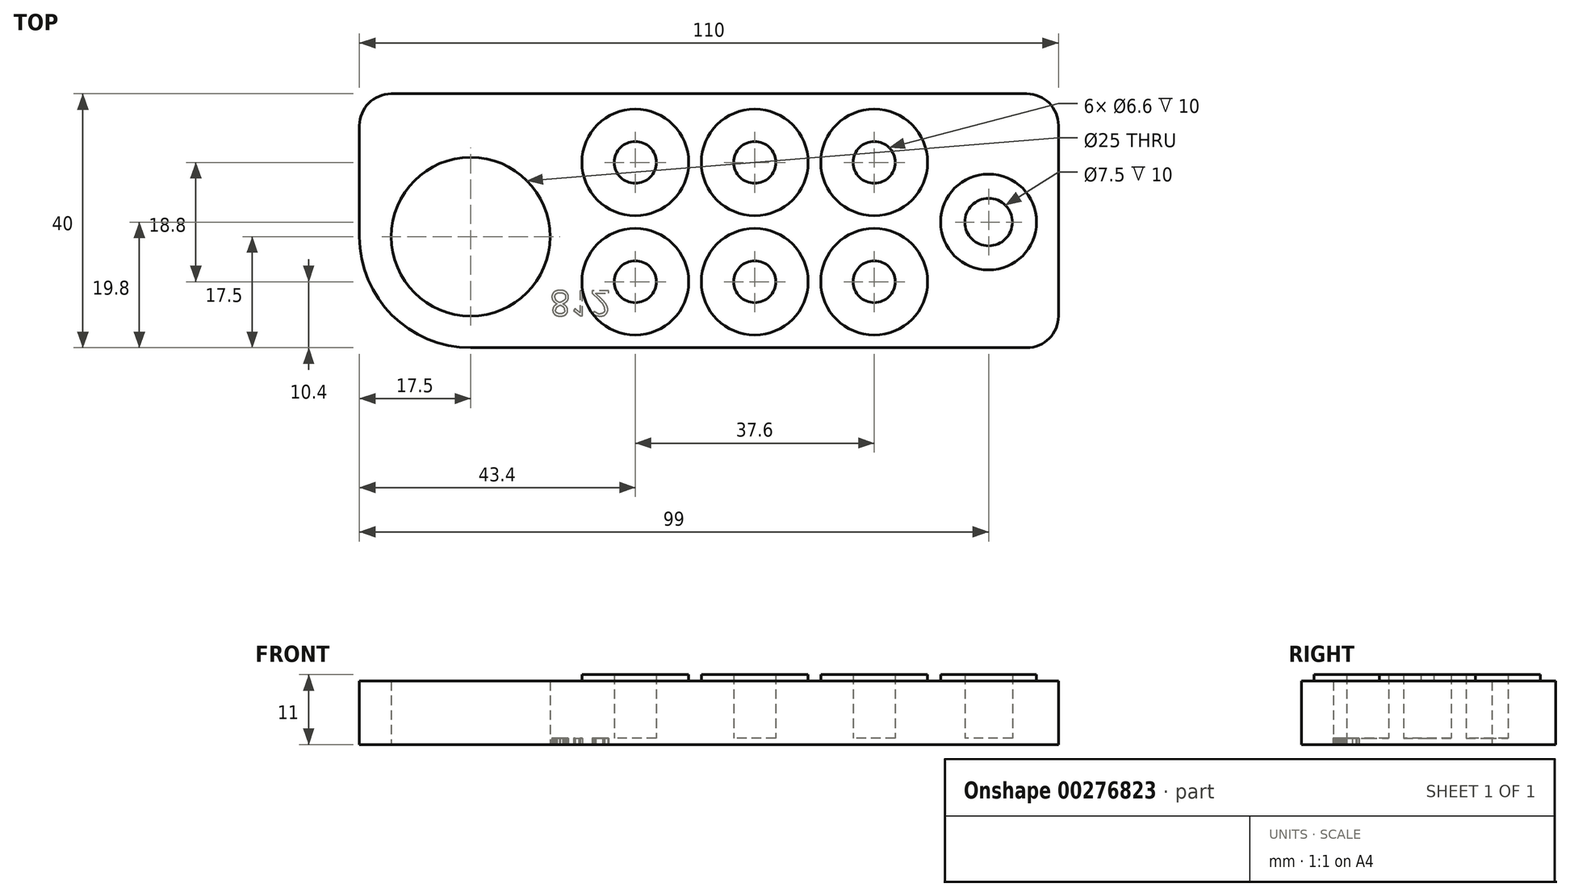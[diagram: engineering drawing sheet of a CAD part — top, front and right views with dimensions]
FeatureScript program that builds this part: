
annotation { "Feature Type Name" : "Feature", "Feature Type Description" : "" }
export const myFeature = defineFeature(function(context is Context, id is Id, definition is map)
    precondition{}
    {
        {
            var Q0;
            Q0=qCreatedBy(makeId("Top.planeOp"),FACE);
            var sketch = newSketch(context, id + "F0", { "sketchPlane" : qUnion([Q0])});
            skLineSegment(sketch, "E0.bottom", {"start": v(17.5, 0) * mm, "end": v(105, 0) * mm});
            skLineSegment(sketch, "E0.top", {"start": v(5, 40) * mm, "end": v(105, 40) * mm});
            skLineSegment(sketch, "E0.left", {"start": v(0, 17.5) * mm, "end": v(0, 35) * mm});
            skLineSegment(sketch, "E0.right", {"start": v(110, 5) * mm, "end": v(110, 35) * mm});
            skLineSegment(sketch, "E1.bottom", {"start": v(0, 0) * mm, "end": v(17.5, 0) * mm, "construction": true});
            skLineSegment(sketch, "E1.top", {"start": v(0, 17.5) * mm, "end": v(17.5, 17.5) * mm, "construction": true});
            skLineSegment(sketch, "E1.left", {"start": v(0, 0) * mm, "end": v(0, 17.5) * mm, "construction": true});
            skLineSegment(sketch, "E1.right", {"start": v(17.5, 0) * mm, "end": v(17.5, 17.5) * mm, "construction": true});
            skCircle(sketch, "E2", {"center": v(17.5, 17.5) * mm, "radius": 12.5 * mm});
            skPoint(sketch, "E3.visualSharp", {"position": v(0, 0) * mm});
            skArc(sketch, "E3.filletArc", {"start": v(0, 17.5) * mm, "mid": v(5.13, 5.13) * mm, "end": v(17.5, 0) * mm});
            skPoint(sketch, "E4.visualSharp", {"position": v(0, 40) * mm});
            skArc(sketch, "E4.filletArc", {"start": v(5, 40) * mm, "mid": v(1.46, 38.54) * mm, "end": v(0, 35) * mm});
            skPoint(sketch, "E5.visualSharp", {"position": v(110, 40) * mm});
            skArc(sketch, "E5.filletArc", {"start": v(110, 35) * mm, "mid": v(108.54, 38.54) * mm, "end": v(105, 40) * mm});
            skPoint(sketch, "E6.visualSharp", {"position": v(110, 0) * mm});
            skArc(sketch, "E6.filletArc", {"start": v(105, 0) * mm, "mid": v(108.54, 1.46) * mm, "end": v(110, 5) * mm});
            skSolve(sketch);
        }
        {
            var Q0;
            Q0=makeQuery(id+"F0.imprint","IMPRINT",FACE,{"disambiguationData":[TD([[makeQuery(id+"F0.imprint","IMPRINT",EDGE,{"derivedFrom":sQuery(id+"F0.wireOp",EDGE,"E0.bottom")}),1.0]])]});
            extrude(context, id + "F1", {"entities" : qUnion([Q0]), "depth" : 10 * mm});
        }
        {
            var Q0;
            Q0=makeQuery(id+"F1.opExtrude","CAP_FACE",FACE,{"disambiguationData":[OSD([sQuery(id+"F0.wireOp",EDGE,"E0.bottom"),sQuery(id+"F0.wireOp",EDGE,"E0.top"),sQuery(id+"F0.wireOp",EDGE,"E0.left"),sQuery(id+"F0.wireOp",EDGE,"E0.right"),sQuery(id+"F0.wireOp",EDGE,"E2"),sQuery(id+"F0.wireOp",EDGE,"E3.filletArc"),sQuery(id+"F0.wireOp",EDGE,"E4.filletArc"),sQuery(id+"F0.wireOp",EDGE,"E5.filletArc"),sQuery(id+"F0.wireOp",EDGE,"E6.filletArc")])],"isStart":false});
            var sketch = newSketch(context, id + "F2", { "sketchPlane" : qUnion([Q0])});
            skLineSegment(sketch, "E7.bottom", {"start": v(0, 0) * mm, "end": v(43.4, 0) * mm, "construction": true});
            skLineSegment(sketch, "E7.top", {"start": v(0, 10.4) * mm, "end": v(43.4, 10.4) * mm, "construction": true});
            skLineSegment(sketch, "E7.left", {"start": v(0, 0) * mm, "end": v(0, 10.4) * mm, "construction": true});
            skLineSegment(sketch, "E7.right", {"start": v(43.4, 0) * mm, "end": v(43.4, 10.4) * mm, "construction": true});
            skLineSegment(sketch, "E8.bottom", {"start": v(43.4, 10.4) * mm, "end": v(62.2, 10.4) * mm, "construction": true});
            skLineSegment(sketch, "E8.top", {"start": v(43.4, 29.2) * mm, "end": v(62.2, 29.2) * mm, "construction": true});
            skLineSegment(sketch, "E8.left", {"start": v(43.4, 10.4) * mm, "end": v(43.4, 29.2) * mm, "construction": true});
            skLineSegment(sketch, "E8.right", {"start": v(62.2, 10.4) * mm, "end": v(62.2, 29.2) * mm, "construction": true});
            skLineSegment(sketch, "E9.bottom", {"start": v(62.2, 29.2) * mm, "end": v(81, 29.2) * mm, "construction": true});
            skLineSegment(sketch, "E9.top", {"start": v(62.2, 10.4) * mm, "end": v(81, 10.4) * mm, "construction": true});
            skLineSegment(sketch, "E9.left", {"start": v(62.2, 29.2) * mm, "end": v(62.2, 10.4) * mm, "construction": true});
            skLineSegment(sketch, "E9.right", {"start": v(81, 29.2) * mm, "end": v(81, 10.4) * mm, "construction": true});
            skPoint(sketch, "E10.oppositeSnap0", {"position": v(81, 19.8) * mm});
            skLineSegment(sketch, "E10.bottom", {"start": v(81, 29.2) * mm, "end": v(99, 29.2) * mm, "construction": true});
            skLineSegment(sketch, "E10.top", {"start": v(81, 19.8) * mm, "end": v(99, 19.8) * mm, "construction": true});
            skLineSegment(sketch, "E10.left", {"start": v(81, 29.2) * mm, "end": v(81, 19.8) * mm, "construction": true});
            skLineSegment(sketch, "E10.right", {"start": v(99, 29.2) * mm, "end": v(99, 19.8) * mm, "construction": true});
            skCircle(sketch, "E11", {"center": v(43.4, 29.2) * mm, "radius": 8.4 * mm});
            skCircle(sketch, "E12", {"center": v(43.4, 10.4) * mm, "radius": 8.4 * mm});
            skCircle(sketch, "E13", {"center": v(62.2, 10.4) * mm, "radius": 8.4 * mm});
            skCircle(sketch, "E14", {"center": v(81, 10.4) * mm, "radius": 8.4 * mm});
            skCircle(sketch, "E15", {"center": v(81, 29.2) * mm, "radius": 8.4 * mm});
            skCircle(sketch, "E16", {"center": v(62.2, 29.2) * mm, "radius": 8.4 * mm});
            skCircle(sketch, "E17", {"center": v(62.2, 29.2) * mm, "radius": 3.3 * mm});
            skCircle(sketch, "E18", {"center": v(81, 29.2) * mm, "radius": 3.3 * mm});
            skCircle(sketch, "E19", {"center": v(81, 10.4) * mm, "radius": 3.3 * mm});
            skCircle(sketch, "E20", {"center": v(62.2, 10.4) * mm, "radius": 3.3 * mm});
            skCircle(sketch, "E21", {"center": v(43.4, 10.4) * mm, "radius": 3.3 * mm});
            skCircle(sketch, "E22", {"center": v(43.4, 29.2) * mm, "radius": 3.3 * mm});
            skCircle(sketch, "E23", {"center": v(99, 19.8) * mm, "radius": 7.55 * mm});
            skCircle(sketch, "E24", {"center": v(99, 19.8) * mm, "radius": 3.75 * mm});
            skSolve(sketch);
        }
        {
            var Q0;
            Q0=makeQuery(id+"F2.imprint","IMPRINT",FACE,{"disambiguationData":[TD([[makeQuery(id+"F2.imprint","IMPRINT",EDGE,{"derivedFrom":sQuery(id+"F2.wireOp",EDGE,"E11")}),1.0]])]});
            var Q1;
            Q1=makeQuery(id+"F2.imprint","IMPRINT",FACE,{"disambiguationData":[TD([[makeQuery(id+"F2.imprint","IMPRINT",EDGE,{"derivedFrom":sQuery(id+"F2.wireOp",EDGE,"E16")}),1.0]])]});
            var Q2;
            Q2=makeQuery(id+"F2.imprint","IMPRINT",FACE,{"disambiguationData":[TD([[makeQuery(id+"F2.imprint","IMPRINT",EDGE,{"derivedFrom":sQuery(id+"F2.wireOp",EDGE,"E13")}),1.0]])]});
            var Q3;
            Q3=makeQuery(id+"F2.imprint","IMPRINT",FACE,{"disambiguationData":[TD([[makeQuery(id+"F2.imprint","IMPRINT",EDGE,{"derivedFrom":sQuery(id+"F2.wireOp",EDGE,"E12")}),1.0]])]});
            var Q4;
            Q4=makeQuery(id+"F2.imprint","IMPRINT",FACE,{"disambiguationData":[TD([[makeQuery(id+"F2.imprint","IMPRINT",EDGE,{"derivedFrom":sQuery(id+"F2.wireOp",EDGE,"E14")}),1.0]])]});
            var Q5;
            Q5=makeQuery(id+"F2.imprint","IMPRINT",FACE,{"disambiguationData":[TD([[makeQuery(id+"F2.imprint","IMPRINT",EDGE,{"derivedFrom":sQuery(id+"F2.wireOp",EDGE,"E15")}),1.0]])]});
            var Q6;
            Q6=makeQuery(id+"F2.imprint","IMPRINT",FACE,{"disambiguationData":[TD([[makeQuery(id+"F2.imprint","IMPRINT",EDGE,{"derivedFrom":sQuery(id+"F2.wireOp",EDGE,"E23")}),1.0]])]});
            extrude(context, id + "F3", {"entities" : qUnion([Q0, Q1, Q2, Q3, Q4, Q5, Q6]), "operationType" : NewBodyOperationType.ADD, "depth" : 1 * mm});
        }
        {
            var Q0;
            Q0=makeQuery(id+"F2.imprint","IMPRINT",FACE,{"disambiguationData":[TD([[makeQuery(id+"F2.imprint","IMPRINT",EDGE,{"derivedFrom":sQuery(id+"F2.wireOp",EDGE,"E24")}),1.0]])]});
            var Q1;
            Q1=makeQuery(id+"F2.imprint","IMPRINT",FACE,{"disambiguationData":[TD([[makeQuery(id+"F2.imprint","IMPRINT",EDGE,{"derivedFrom":sQuery(id+"F2.wireOp",EDGE,"E18")}),1.0]])]});
            var Q2;
            Q2=makeQuery(id+"F2.imprint","IMPRINT",FACE,{"disambiguationData":[TD([[makeQuery(id+"F2.imprint","IMPRINT",EDGE,{"derivedFrom":sQuery(id+"F2.wireOp",EDGE,"E19")}),1.0]])]});
            var Q3;
            Q3=makeQuery(id+"F2.imprint","IMPRINT",FACE,{"disambiguationData":[TD([[makeQuery(id+"F2.imprint","IMPRINT",EDGE,{"derivedFrom":sQuery(id+"F2.wireOp",EDGE,"E20")}),1.0]])]});
            var Q4;
            Q4=makeQuery(id+"F2.imprint","IMPRINT",FACE,{"disambiguationData":[TD([[makeQuery(id+"F2.imprint","IMPRINT",EDGE,{"derivedFrom":sQuery(id+"F2.wireOp",EDGE,"E17")}),1.0]])]});
            var Q5;
            Q5=makeQuery(id+"F2.imprint","IMPRINT",FACE,{"disambiguationData":[TD([[makeQuery(id+"F2.imprint","IMPRINT",EDGE,{"derivedFrom":sQuery(id+"F2.wireOp",EDGE,"E22")}),1.0]])]});
            var Q6;
            Q6=makeQuery(id+"F2.imprint","IMPRINT",FACE,{"disambiguationData":[TD([[makeQuery(id+"F2.imprint","IMPRINT",EDGE,{"derivedFrom":sQuery(id+"F2.wireOp",EDGE,"E21")}),1.0]])]});
            extrude(context, id + "F4", {"entities" : qUnion([Q0, Q1, Q2, Q3, Q4, Q5, Q6]), "operationType" : NewBodyOperationType.REMOVE, "oppositeDirection" : true, "depth" : 9 * mm});
        }
        {
            var Q0;
            Q0=makeQuery(id+"F1.opExtrude","CAP_FACE",FACE,{"disambiguationData":[OSD([sQuery(id+"F0.wireOp",EDGE,"E0.bottom"),sQuery(id+"F0.wireOp",EDGE,"E0.top"),sQuery(id+"F0.wireOp",EDGE,"E0.left"),sQuery(id+"F0.wireOp",EDGE,"E0.right"),sQuery(id+"F0.wireOp",EDGE,"E2"),sQuery(id+"F0.wireOp",EDGE,"E3.filletArc"),sQuery(id+"F0.wireOp",EDGE,"E4.filletArc"),sQuery(id+"F0.wireOp",EDGE,"E5.filletArc"),sQuery(id+"F0.wireOp",EDGE,"E6.filletArc")])],"isStart":true});
            var sketch = newSketch(context, id + "F5", { "sketchPlane" : qUnion([Q0])});
            skLineSegment(sketch, "E25.bottom", {"start": v(0, 0) * mm, "end": v(30, 0) * mm, "construction": true});
            skLineSegment(sketch, "E25.top", {"start": v(0, -5) * mm, "end": v(30, -5) * mm, "construction": true});
            skLineSegment(sketch, "E25.left", {"start": v(0, 0) * mm, "end": v(0, -5) * mm, "construction": true});
            skLineSegment(sketch, "E25.right", {"start": v(30, 0) * mm, "end": v(30, -5) * mm, "construction": true});
            skText(sketch, "E26", { "text": "812", "fontName": "OpenSans-Regular.ttf"});
            const initialGuessF5  = {"E26": [0.03, -0.009, 1, 0, 0.004]};
            skSetInitialGuess(sketch, initialGuessF5);
            skSolve(sketch);
        }
        {
            var Q0;
            Q0 = qSketchRegion(id + "F5", true);
            extrude(context, id + "F6", {"entities" : qUnion([Q0]), "operationType" : NewBodyOperationType.REMOVE, "oppositeDirection" : true, "depth" : 1 * mm});
        }
    });
